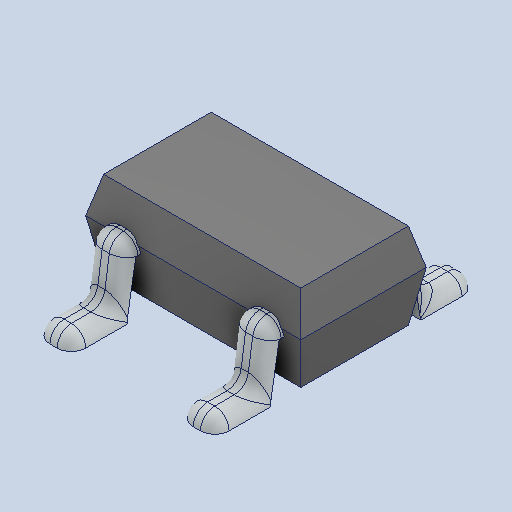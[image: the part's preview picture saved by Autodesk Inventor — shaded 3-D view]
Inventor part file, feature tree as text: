
AUTODESK INVENTOR PART (.ipt)
format: ipt  version: 2024 (Build 280153000, 153)  size: 248,320 bytes
history: native  units: in
note: dims shown in document units (in); Inventor stores cm internally (conversion verified against a paired STEP export)
features: fillet x1
ambient origin geometry x8: Origin, YZ Plane, XZ Plane, XY Plane, X Axis, Y Axis, Z Axis, Center Point
bodies: Solid1 (feature_tree)
feature tree (1):
  fillet  "Fillet6"  [1 undecoded]
note: 1 required parameter value undecoded (feature->parameter linkage not recoverable at this tier; creation-order binding heuristic only, values carry confidence <= 0.55)
